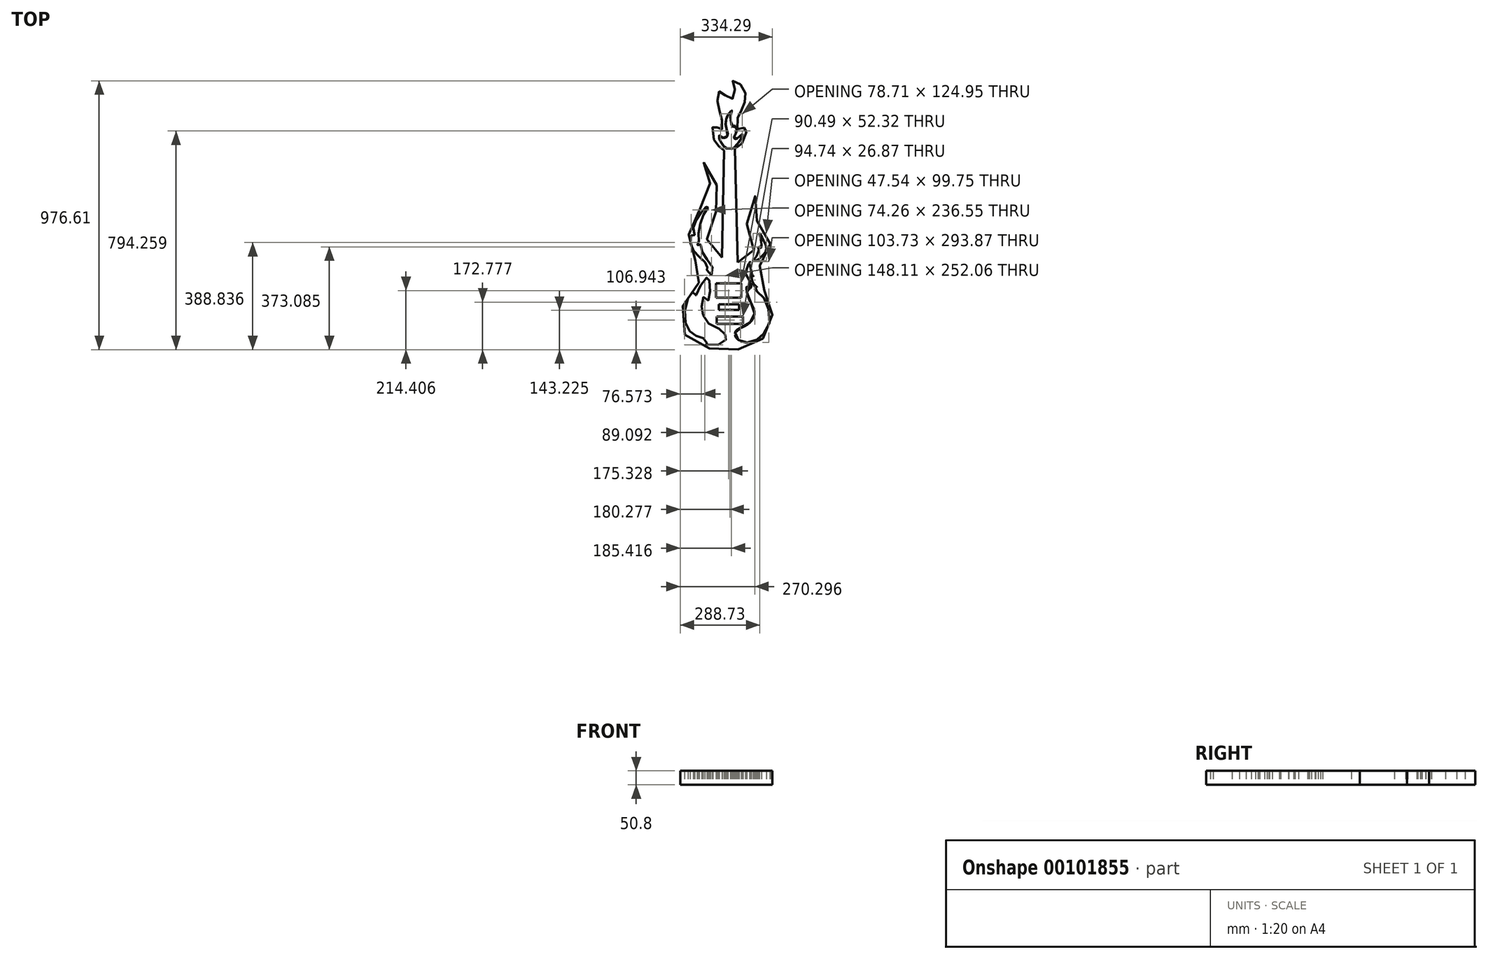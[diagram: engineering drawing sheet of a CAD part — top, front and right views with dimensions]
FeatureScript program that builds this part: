
annotation { "Feature Type Name" : "Feature", "Feature Type Description" : "" }
export const myFeature = defineFeature(function(context is Context, id is Id, definition is map)
    precondition{}
    {
        {
            var Q0;
            Q0=qCreatedBy(makeId("Top.planeOp"),FACE);
            var sketch = newSketch(context, id + "F0", { "sketchPlane" : qUnion([Q0])});
            skFitSpline(sketch, "E0", {"points": [v(-26.78, -24.95) * mm, v(-62.13, 0) * mm, v(-81.92, 54.23) * mm, v(-55.06, 126.35) * mm, v(-36.68, 187.15) * mm, v(-49.4, 247.95) * mm, v(-73.44, 297.44) * mm, v(-100.94, 322.73) * mm, v(-73.65, 257.85) * mm, v(-76.8, 194.47) * mm, v(-117.54, 138.64) * mm, v(-144.14, 72.62) * mm, v(-146.97, 0) * mm, v(-114.44, -48.99) * mm, v(-98.9, -95.65) * mm, v(-131.41, -139.48) * mm, v(-169.59, -201.7) * mm, v(-175.25, -273.8) * mm, v(-134.24, -334.61) * mm, v(-67.78, -355.82) * mm, v(0, -360.06) * mm, v(70.79, -353) * mm, v(121.7, -319.06) * mm, v(148.56, -279.47) * mm, v(154.21, -205.94) * mm, v(134.42, -156.45) * mm, v(108.96, -112.62) * mm, v(111.8, -54.64) * mm, v(147.14, -13.64) * mm, v(140.07, 48.58) * mm, v(107.55, 95.24) * mm, v(89.17, 158.87) * mm, v(93.2, 197.05) * mm, v(57.85, 126.35) * mm, v(83.51, 62.72) * mm, v(87.76, 0) * mm, v(59.77, -33.38) * mm, v(29.78, -43.33) * mm], "startDerivative": vector(-1627.35, 865.84) * mm, "endDerivative": vector(-1459.23, -353.54) * mm});
            skFitSpline(sketch, "E1", {"points": [v(20.03, 369.26) * mm, v(51.2, 398.9) * mm, v(59.77, 448.37) * mm, v(32.89, 437.1) * mm, v(31.56, 483.77) * mm, v(48.6, 517.67) * mm, v(58.56, 554.42) * mm, v(45.92, 596.86) * mm, v(12.02, 615.31) * mm, v(21.83, 570.04) * mm, v(0, 550.3) * mm, v(-31.88, 580.05) * mm, v(-43.25, 550.37) * mm, v(-33.45, 499.45) * mm, v(-25.05, 455.6) * mm, v(-32.16, 435.82) * mm, v(-56.16, 455.66) * mm, v(-57.67, 406.18) * mm, v(-36.52, 376.44) * mm, v(-19.57, 363.68) * mm, v(20.03, 369.26) * mm]});
            skLineSegment(sketch, "E2", {"start": v(-19.57, 363.68) * mm, "end": v(-26.78, -24.95) * mm});
            skLineSegment(sketch, "E3", {"start": v(20.03, 369.26) * mm, "end": v(29.78, -43.33) * mm});
            skLineSegment(sketch, "E4", {"start": v(-26.78, -24.95) * mm, "end": v(-26.78, -102.72) * mm});
            skLineSegment(sketch, "E5", {"start": v(-26.78, -102.72) * mm, "end": v(29.78, -102.72) * mm});
            skLineSegment(sketch, "E6", {"start": v(29.78, -102.72) * mm, "end": v(29.78, -43.33) * mm});
            skLineSegment(sketch, "E7.bottom", {"start": v(-48.2, -119.69) * mm, "end": v(42.3, -119.69) * mm});
            skLineSegment(sketch, "E7.top", {"start": v(-48.2, -172) * mm, "end": v(42.3, -172) * mm});
            skLineSegment(sketch, "E7.left", {"start": v(-48.2, -119.69) * mm, "end": v(-48.2, -172) * mm});
            skLineSegment(sketch, "E7.right", {"start": v(42.3, -119.69) * mm, "end": v(42.3, -172) * mm});
            skLineSegment(sketch, "E8.bottom", {"start": v(-38.3, -196.04) * mm, "end": v(35.46, -196.04) * mm});
            skLineSegment(sketch, "E8.top", {"start": v(-38.3, -215.46) * mm, "end": v(35.46, -215.46) * mm});
            skLineSegment(sketch, "E8.left", {"start": v(-38.3, -196.04) * mm, "end": v(-38.3, -215.46) * mm});
            skLineSegment(sketch, "E8.right", {"start": v(35.46, -196.04) * mm, "end": v(35.46, -215.46) * mm});
            skLineSegment(sketch, "E9.bottom", {"start": v(-45.37, -239.87) * mm, "end": v(49.37, -239.87) * mm});
            skLineSegment(sketch, "E9.top", {"start": v(-45.37, -266.74) * mm, "end": v(49.37, -266.74) * mm});
            skLineSegment(sketch, "E9.left", {"start": v(-45.37, -239.87) * mm, "end": v(-45.37, -266.74) * mm});
            skLineSegment(sketch, "E9.right", {"start": v(49.37, -239.87) * mm, "end": v(49.37, -266.74) * mm});
            skFitSpline(sketch, "E10", {"points": [v(-15.13, -305.4) * mm, v(-27.56, -288.7) * mm, v(-63.81, -275.37) * mm, v(-90.23, -245.85) * mm, v(-97.48, -226.17) * mm, v(-100.59, -198.2) * mm, v(-94.89, -171.1) * mm, v(-86.6, -166.09) * mm, v(-75.73, -181.63) * mm, v(-70.03, -153.14) * mm, v(-71.58, -116.89) * mm, v(-79.87, -91) * mm, v(-86.08, -109.12) * mm, v(-108.87, -132.42) * mm, v(-122.34, -164.54) * mm, v(-127.52, -167.48) * mm, v(-135.8, -147.96) * mm, v(-149.79, -171.62) * mm, v(-162.22, -219.95) * mm, v(-158.07, -266.05) * mm, v(-144.09, -291.3) * mm, v(-142.54, -296.08) * mm, v(-121.3, -309.55) * mm, v(-108.87, -315.76) * mm, v(-81.94, -323.01) * mm, v(-79.87, -334.93) * mm, v(-95.4, -337.52) * mm, v(-67.96, -344.77) * mm, v(-31.19, -339.07) * mm, v(-12.02, -323.53) * mm, v(-9.95, -312.66) * mm, v(-15.13, -305.4) * mm]});
            skFitSpline(sketch, "E11", {"points": [v(64.1, -334.4) * mm, v(93.63, -327.68) * mm, v(111.24, -317.32) * mm, v(126.78, -300.23) * mm, v(145.42, -262.42) * mm, v(142.83, -214.25) * mm, v(128.85, -176.45) * mm, v(111.24, -157.8) * mm, v(92.6, -141.75) * mm, v(87.93, -130.87) * mm, v(99.33, -132.94) * mm, v(88.97, -122.58) * mm, v(80.16, -107.05) * mm, v(78.1, -89.44) * mm, v(89.49, -94.62) * mm, v(80.16, -78.56) * mm, v(73.95, -59.92) * mm, v(76.02, -50.08) * mm, v(76.54, -39.72) * mm, v(64.63, -57.33) * mm, v(57.9, -80.12) * mm, v(66.18, -101.87) * mm, v(79.13, -121.55) * mm, v(73.95, -139.16) * mm, v(63.6, -130.87) * mm, v(64.1, -155.21) * mm, v(77.06, -187.84) * mm, v(90, -216.84) * mm, v(86.38, -247.4) * mm, v(68.77, -266.56) * mm, v(46.5, -279) * mm, v(28.37, -287.28) * mm, v(20.09, -301.78) * mm, v(27.86, -320.94) * mm, v(42.36, -328.71) * mm, v(64.1, -334.4) * mm]});
            skFitSpline(sketch, "E12", {"points": [v(-64.58, -89.69) * mm, v(-59.64, -73.56) * mm, v(-67.86, -48.5) * mm, v(-86.25, -25.63) * mm, v(-97.92, -7.7) * mm, v(-102.45, 15.6) * mm, v(-105.42, 21.65) * mm, v(-109.58, 12.17) * mm, v(-117.13, 24.38) * mm, v(-115.1, 37.02) * mm, v(-109.87, 34.28) * mm, v(-111.25, 51.08) * mm, v(-110, 78.57) * mm, v(-102.08, 108.99) * mm, v(-92.5, 131.49) * mm, v(-82.9, 149) * mm, v(-73.23, 166.6) * mm, v(-85, 157.75) * mm, v(-99.57, 141.5) * mm, v(-109.59, 128.99) * mm, v(-121.25, 109.83) * mm, v(-130.44, 89) * mm, v(-129.17, 66.92) * mm, v(-126.6, 53.98) * mm, v(-131.65, 45.93) * mm, v(-139.2, 54.94) * mm, v(-141.68, 35.64) * mm, v(-137.1, 15.22) * mm, v(-127.5, -4.79) * mm, v(-113.33, -19.37) * mm, v(-97.48, -35.2) * mm, v(-83.37, -47.29) * mm, v(-76.37, -61.15) * mm, v(-88.83, -60.47) * mm, v(-84.97, -68.91) * mm, v(-71.6, -77.89) * mm, v(-64.58, -89.69) * mm]});
            skFitSpline(sketch, "E13", {"points": [v(86.68, -37.04) * mm, v(102.7, -34.8) * mm, v(118.9, -18.96) * mm, v(131, -5.72) * mm, v(133.77, 12.37) * mm, v(126.88, 31.04) * mm, v(125.36, 33.59) * mm, v(117.54, 50.64) * mm, v(109.23, 62.68) * mm, v(113.79, 41.06) * mm, v(116.28, 19.8) * mm, v(113.37, 7.79) * mm, v(105.42, 13.92) * mm, v(106.08, 3.5) * mm, v(102.12, -11.57) * mm, v(93.64, -28.2) * mm, v(86.68, -37.04) * mm]});
            skFitSpline(sketch, "E14", {"points": [v(14.79, 371.54) * mm, v(26.37, 383.64) * mm, v(37.42, 397.32) * mm, v(43.81, 410.9) * mm, v(46.98, 422.76) * mm, v(39.12, 415.42) * mm, v(28.5, 407.24) * mm, v(21.32, 404.79) * mm, v(16.78, 410.15) * mm, v(19.64, 421.6) * mm, v(21.42, 421.52) * mm, v(28.26, 430.81) * mm, v(27.2, 438.53) * mm, v(22.09, 443.53) * mm, v(22.14, 448.09) * mm, v(18.68, 457.16) * mm, v(16.08, 449.33) * mm, v(11.47, 450.16) * mm, v(6.21, 461.85) * mm, v(3.56, 476.16) * mm, v(4.88, 492.86) * mm, v(7.92, 504.43) * mm, v(8.68, 508.78) * mm, v(-4.5, 493.74) * mm, v(-9.6, 482.46) * mm, v(-13.66, 464.75) * mm, v(-13.38, 454.7) * mm, v(-11, 441.97) * mm, v(-6.01, 428.44) * mm, v(-7.9, 414.42) * mm, v(-16.33, 408.88) * mm, v(-26.1, 409.41) * mm, v(-33.6, 415.46) * mm, v(-37.4, 417.2) * mm, v(-35.38, 403.54) * mm, v(-28.23, 388.95) * mm, v(-18.4, 375.68) * mm, v(-12.6, 371.24) * mm, v(-3.09, 370.93) * mm, v(14.79, 371.54) * mm]});
            skSolve(sketch);
        }
        {
            var Q0;
            Q0 = qSketchRegion(id + "F0", true);
            extrude(context, id + "F1", {"entities" : qUnion([Q0]), "depth" : 50.8 * mm});
        }
    });
